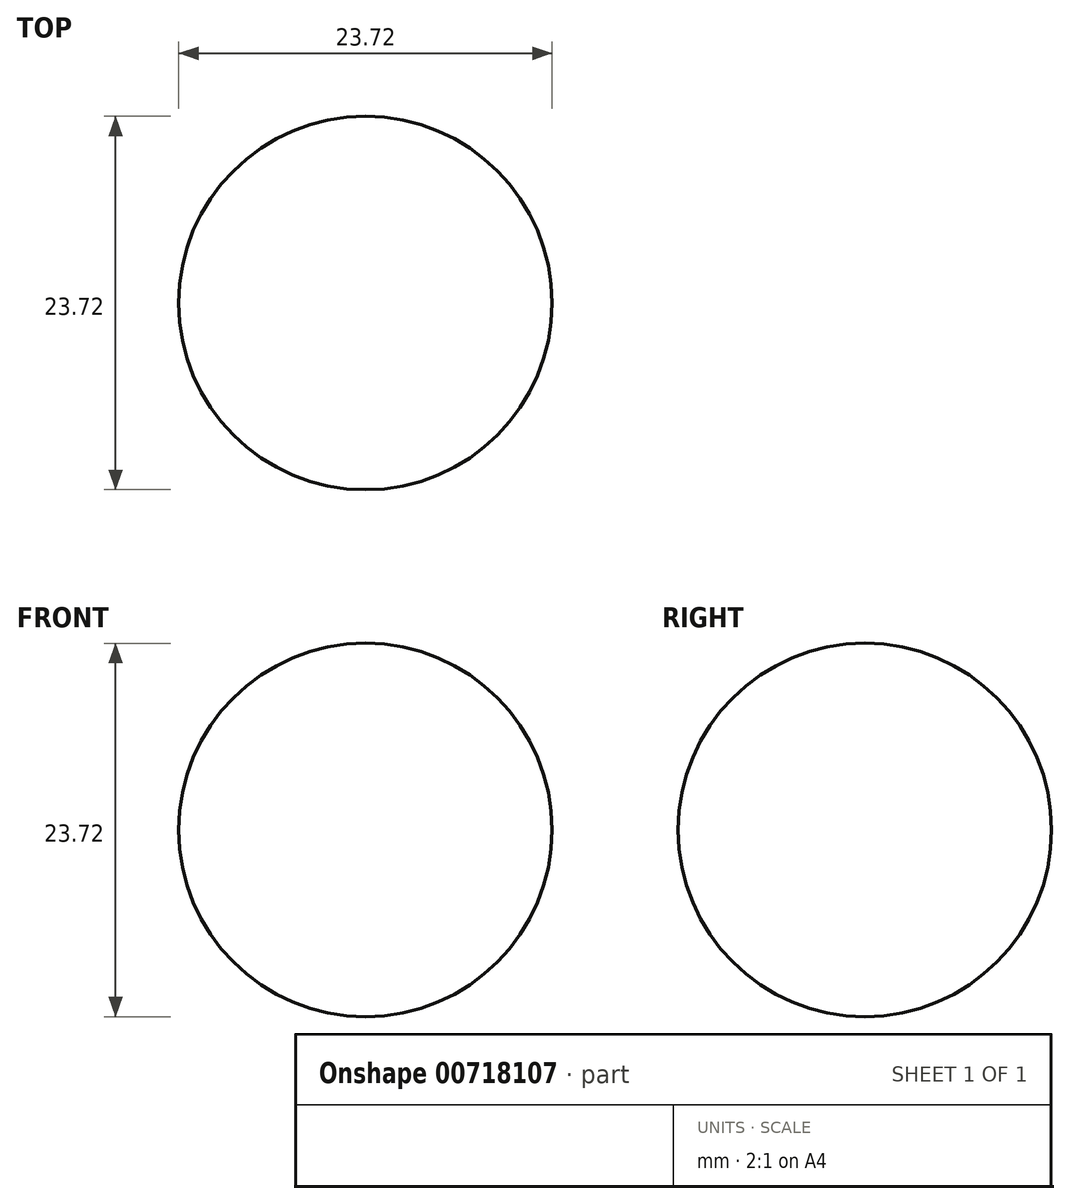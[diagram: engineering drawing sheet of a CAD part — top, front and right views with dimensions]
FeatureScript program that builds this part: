
annotation { "Feature Type Name" : "Feature", "Feature Type Description" : "" }
export const myFeature = defineFeature(function(context is Context, id is Id, definition is map)
    precondition{}
    {
        {
            var Q0;
            Q0=qCreatedBy(makeId("Top.planeOp"),FACE);
            var sketch = newSketch(context, id + "F0", { "sketchPlane" : qUnion([Q0])});
            skCircle(sketch, "E0", {"center": v(0, 0) * mm, "radius": 11.86 * mm});
            skLineSegment(sketch, "E1", {"start": v(0, 11.86) * mm, "end": v(0, -11.86) * mm});
            skSolve(sketch);
        }
        {
            var Q0;
            {var subQ0=sQuery(id+"F0.wireOp",EDGE,"E1");Q0=makeQuery(id+"F0.imprint","IMPRINT",FACE,{"disambiguationData":[TD([[makeQuery(id+"F0.imprint","IMPRINT",EDGE,{"derivedFrom":subQ0}),1.0]])]});}
            var Q1;
            Q1=sQuery(id+"F0.wireOp",EDGE,"E1");
            revolve(context, id + "F1", {"surfaceOperationType" : NewSurfaceOperationType.NEW, "entities" : qUnion([Q0]), "axis" : qUnion([Q1]), "revolveType" : RevolveType.FULL});
        }
    });
